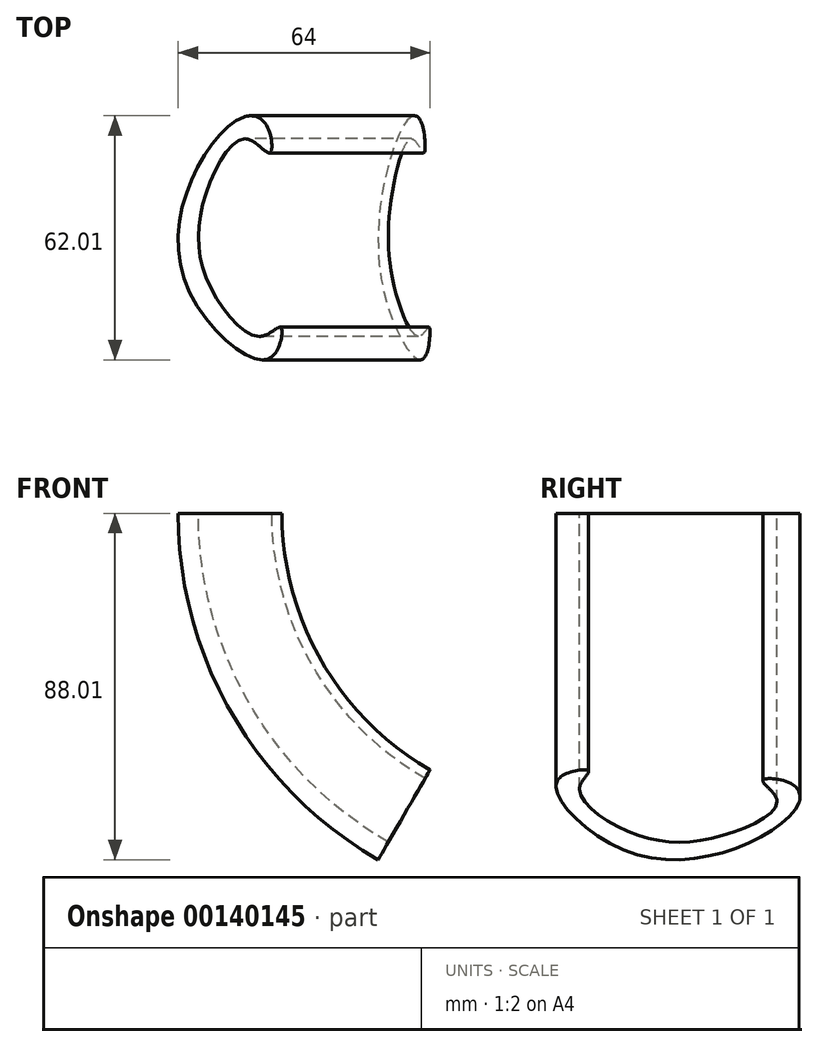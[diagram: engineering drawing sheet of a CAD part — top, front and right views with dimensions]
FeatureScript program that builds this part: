
annotation { "Feature Type Name" : "Feature", "Feature Type Description" : "" }
export const myFeature = defineFeature(function(context is Context, id is Id, definition is map)
    precondition{}
    {
        {
            var Q0;
            Q0=qCreatedBy(makeId("Top.planeOp"),FACE);
            var sketch = newSketch(context, id + "F0", { "sketchPlane" : qUnion([Q0])});
            skLineSegment(sketch, "E0", {"start": v(-11.63, 0) * mm, "end": v(-11.63, 0) * mm});
            skFitSpline(sketch, "E1", {"points": [v(3.88, 24.09) * mm, v(-8.81, 9.46) * mm, v(-10.6, -18.97) * mm, v(6.8, -37.37) * mm, v(12.28, -35.32) * mm, v(13.2, -29.39) * mm, v(8.18, -31.67) * mm, v(-5.05, -18.22) * mm, v(-5.96, 3.9) * mm, v(4.53, 18.49) * mm, v(10.42, 14.94) * mm, v(9.77, 21.68) * mm, v(3.88, 24.09) * mm]});
            skLineSegment(sketch, "E2", {"start": v(88.8, 42.5) * mm, "end": v(88.8, -46.06) * mm, "construction": true});
            skSolve(sketch);
        }
        {
            var Q0;
            Q0=makeQuery(id+"F0.imprint","IMPRINT",FACE,{"disambiguationData":[TD([[makeQuery(id+"F0.imprint","IMPRINT",EDGE,{"derivedFrom":sQuery(id+"F0.wireOp",EDGE,"E1")}),1.0]])]});
            var Q1;
            Q1 = qConstructionFilter(qBodyType(qCreatedBy(id + "F0" ,EDGE), BodyType.WIRE), ConstructionObject.NO);
            var Q2;
            Q2=sQuery(id+"F0.wireOp",EDGE,"E2");
            revolve(context, id + "F1", {"entities" : qUnion([Q0]), "surfaceEntities" : qUnion([Q1]), "axis" : qUnion([Q2]), "revolveType" : RevolveType.ONE_DIRECTION, "angle" : 60 * degree});
        }
    });
